# Revit family: STS-747 Аудиодомофонная панель_RV17_LOD400
name_source: partatom
category: Электрооборудование
revit_build: Autodesk Revit 2017 (Build: 20170118_1100(x64)
units: mm (PartAtom-declared; Revit-internal decimal feet)

## family parameters
Всегда вертикально = Да
Конфигурация панели = Два столбца, слева направо
На основе рабочей плоскости = Нет
Общий = Нет
При загрузке вырезать с полостями = Нет
Размер круглого соединителя = Использовать диаметр
Тип детали = Щит
Точка расчета площади = Нет

## types (1)
- STS-747
    ADSK_URL страницы изделия = https://stilsoft.ru
    ADSK_Единица измерения = шт.
    ADSK_Завод-изготовитель = ООО «Основа Безопасности»
    ADSK_Количество = 1
    ADSK_Марка = СТВФ.431295.016
    ADSK_Масса = 1.4
    ADSK_Наименование = STS-747 Аудиодомофонная панель
    ADSK_Размер_Высота = 162 мм
    ADSK_Размер_Глубина = 60 мм
    ADSK_Размер_Ширина = 92 мм
    Интерфейс связи = 10BaseT/100BaseT X Ethernet
    Максимальный потребляемый ток, А = 0 А
    Мощность = 3
    Напряжение = 12
    Режим работы = непрерывный
